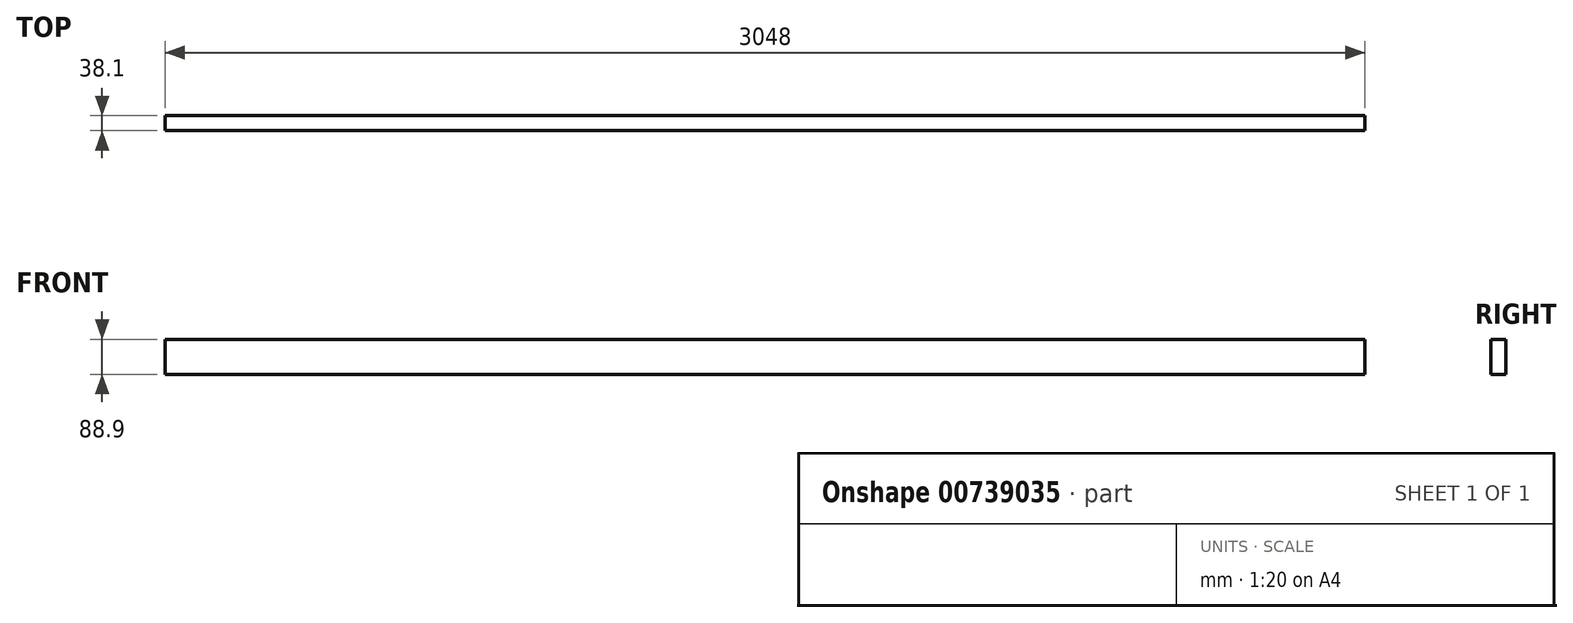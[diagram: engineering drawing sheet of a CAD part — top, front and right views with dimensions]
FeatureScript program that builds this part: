
annotation { "Feature Type Name" : "Feature", "Feature Type Description" : "" }
export const myFeature = defineFeature(function(context is Context, id is Id, definition is map)
    precondition{}
    {
        {
            var Q0;
            Q0=qCreatedBy(makeId("Front.planeOp"),FACE);
            var sketch = newSketch(context, id + "F0", { "sketchPlane" : qUnion([Q0])});
            skLineSegment(sketch, "E0.bottom", {"start": v(0, 0) * mm, "end": v(3048, 0) * mm});
            skLineSegment(sketch, "E0.top", {"start": v(0, 88.9) * mm, "end": v(3048, 88.9) * mm});
            skLineSegment(sketch, "E0.left", {"start": v(0, 0) * mm, "end": v(0, 88.9) * mm});
            skLineSegment(sketch, "E0.right", {"start": v(3048, 0) * mm, "end": v(3048, 88.9) * mm});
            skSolve(sketch);
        }
        {
            var Q0;
            Q0 = qSketchRegion(id + "F0", true);
            extrude(context, id + "F1", {"entities" : qUnion([Q0]), "depth" : 38.1 * mm, "offsetDistance" : 25.4 * mm});
        }
    });
